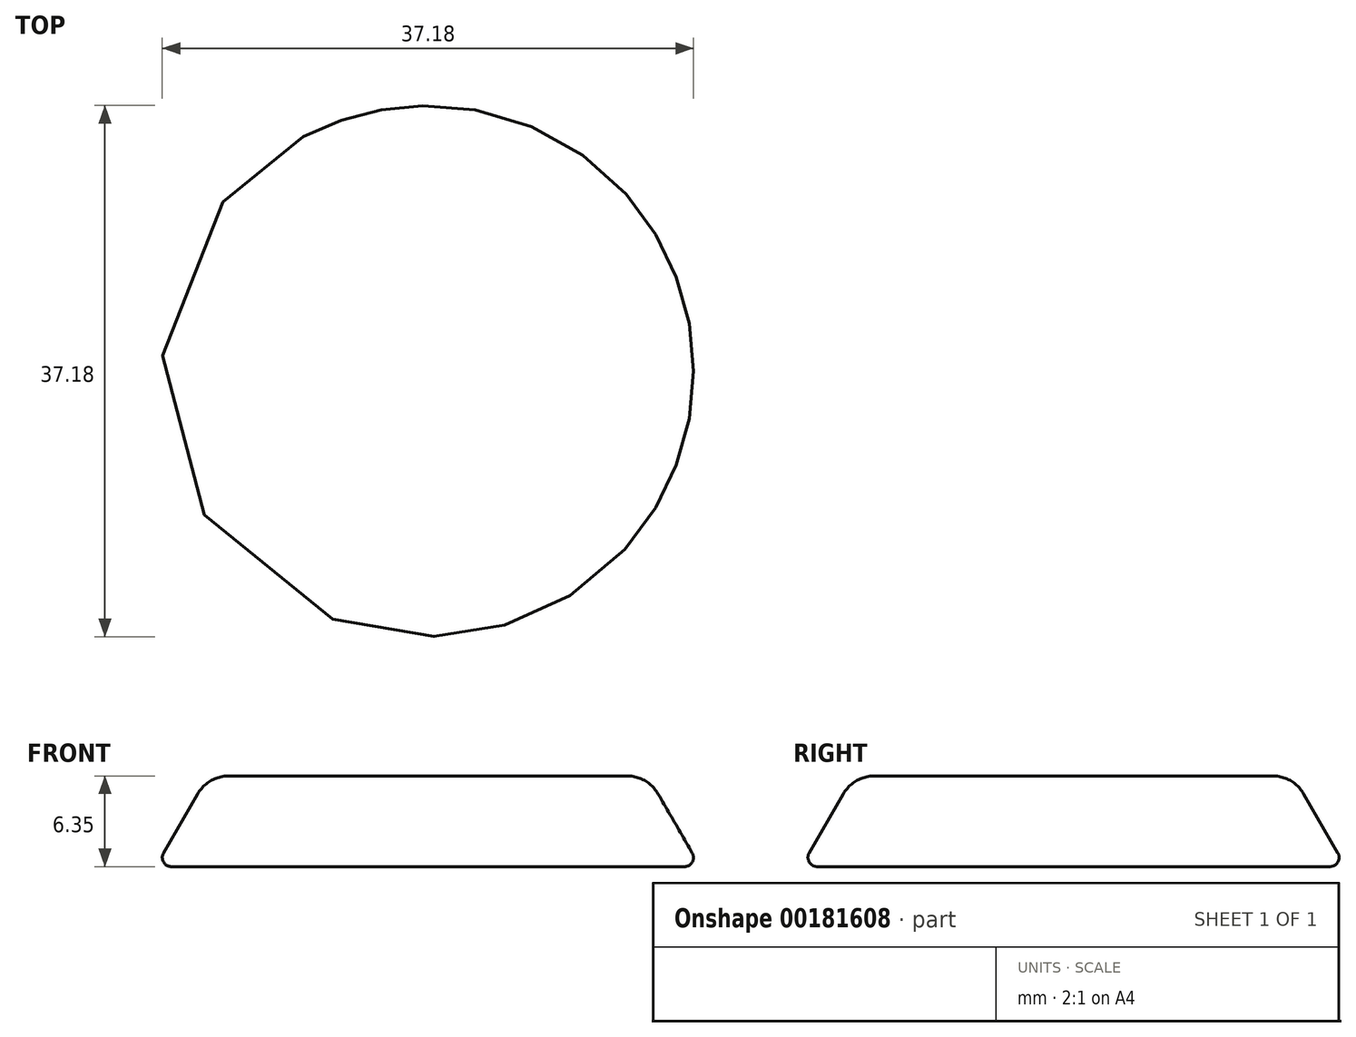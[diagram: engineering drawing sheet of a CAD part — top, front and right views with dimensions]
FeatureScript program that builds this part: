
annotation { "Feature Type Name" : "Feature", "Feature Type Description" : "" }
export const myFeature = defineFeature(function(context is Context, id is Id, definition is map)
    precondition{}
    {
        {
            var Q0;
            Q0=qCreatedBy(makeId("Top.planeOp"),FACE);
            var sketch = newSketch(context, id + "F0", { "sketchPlane" : qUnion([Q0])});
            skCircle(sketch, "E0", {"center": v(0, 0) * mm, "radius": 19.05 * mm});
            skSolve(sketch);
        }
        {
            var Q0;
            Q0=makeQuery(id+"F0.imprint","IMPRINT",FACE,{"disambiguationData":[TD([[makeQuery(id+"F0.imprint","IMPRINT",EDGE,{"derivedFrom":sQuery(id+"F0.wireOp",EDGE,"E0")}),1.0]])]});
            extrude(context, id + "F1", {"entities" : qUnion([Q0]), "depth" : 6.35 * mm, "hasDraft" : true, "draftAngle" : 30 * degree, "draftPullDirection" : true});
        }
        {
            var Q0;
            Q0=makeQuery(id+"F1.opExtrude","CAP_EDGE",EDGE,{"disambiguationData":[OSD([sQuery(id+"F0.wireOp",EDGE,"E0")])],"isStart":false});
            fillet(context, id + "F2", {"entities" : qUnion([Q0]), "radius" : 2.54 * mm, "tangentPropagation" : true, "allowEdgeOverflow" : false});
        }
        {
            var Q0;
            Q0=makeQuery(id+"F1.opExtrude","CAP_EDGE",EDGE,{"disambiguationData":[OSD([sQuery(id+"F0.wireOp",EDGE,"E0")])],"isStart":true});
            fillet(context, id + "F3", {"entities" : qUnion([Q0]), "radius" : 0.64 * mm, "tangentPropagation" : true, "allowEdgeOverflow" : false});
        }
    });
